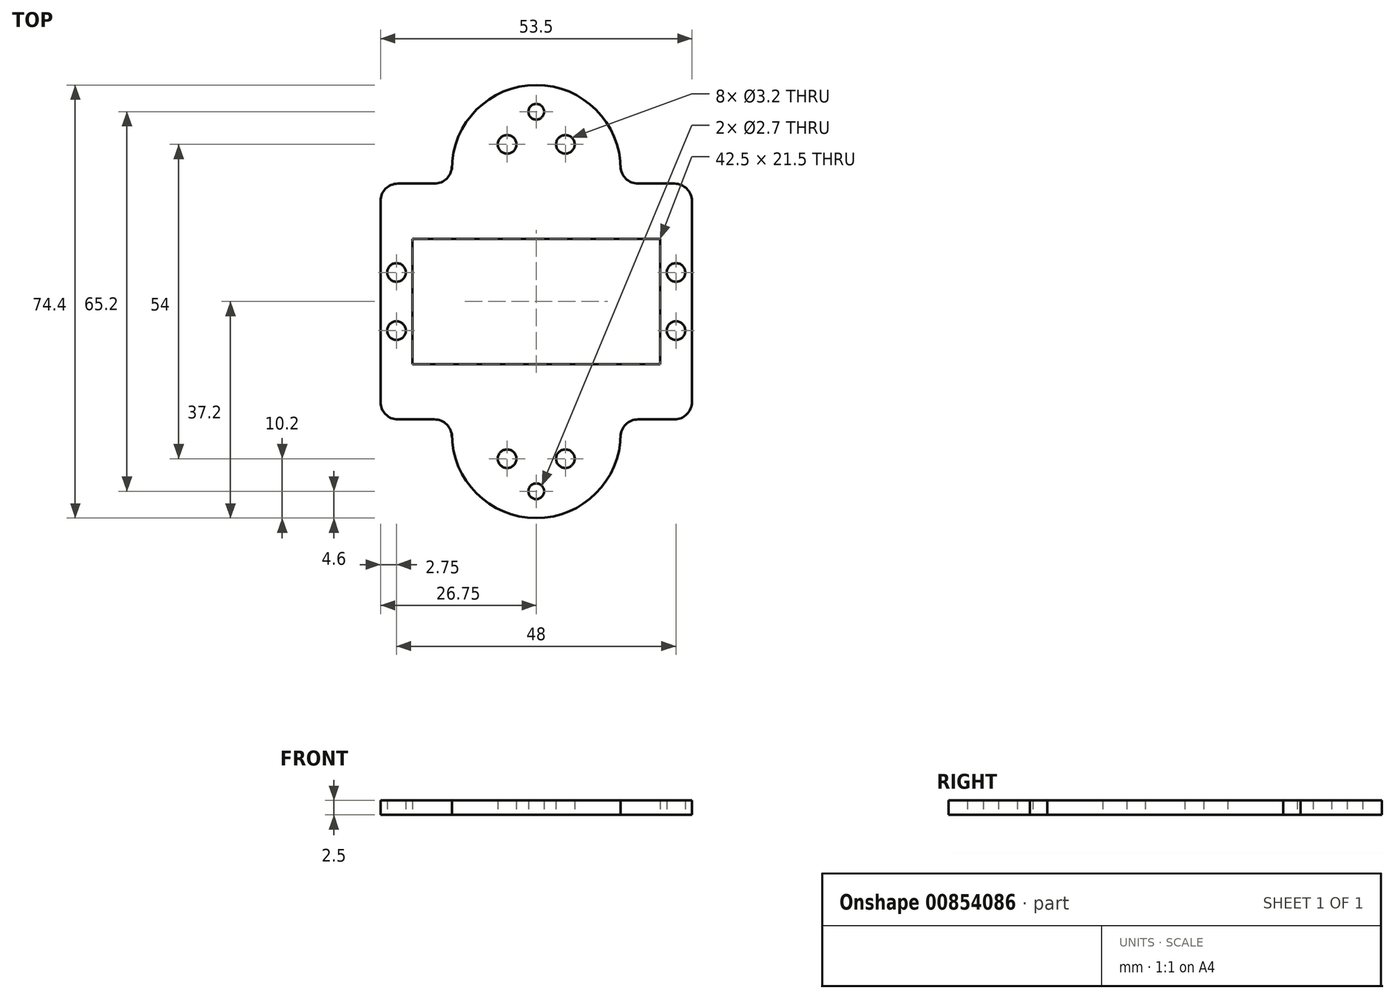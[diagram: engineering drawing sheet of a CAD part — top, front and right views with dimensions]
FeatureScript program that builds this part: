
annotation { "Feature Type Name" : "Feature", "Feature Type Description" : "" }
export const myFeature = defineFeature(function(context is Context, id is Id, definition is map)
    precondition{}
    {
        {
            var Q0;
            Q0=qCreatedBy(makeId("Top.planeOp"),FACE);
            var sketch = newSketch(context, id + "F0", { "sketchPlane" : qUnion([Q0])});
            skLineSegment(sketch, "E0", {"start": v(0, 0) * mm, "end": v(53.5, 0) * mm});
            skLineSegment(sketch, "E1", {"start": v(0, 0) * mm, "end": v(0, 17.25) * mm});
            skLineSegment(sketch, "E2", {"start": v(3, 20.25) * mm, "end": v(9.25, 20.25) * mm});
            skLineSegment(sketch, "E3", {"start": v(12.25, 22.7) * mm, "end": v(12.25, 23.25) * mm});
            skLineSegment(sketch, "E4", {"start": v(26.75, -69.73) * mm, "end": v(26.75, 52.22) * mm});
            skLineSegment(sketch, "E5", {"start": v(12.25, 22.7) * mm, "end": v(26.75, 22.7) * mm});
            skLineSegment(sketch, "E6.MirrorCS", {"start": v(53.5, 0) * mm, "end": v(53.5, 17.25) * mm});
            skLineSegment(sketch, "E7.MirrorCS", {"start": v(50.5, 20.25) * mm, "end": v(44.25, 20.25) * mm});
            skLineSegment(sketch, "E8.MirrorCS", {"start": v(41.25, 22.7) * mm, "end": v(41.25, 23.25) * mm});
            skLineSegment(sketch, "E9.MirrorCS", {"start": v(41.25, 22.7) * mm, "end": v(26.75, 22.7) * mm});
            skLineSegment(sketch, "E10.MirrorCS", {"start": v(0, 0) * mm, "end": v(0, -17.25) * mm});
            skLineSegment(sketch, "E11.MirrorCS", {"start": v(3, -20.25) * mm, "end": v(9.25, -20.25) * mm});
            skLineSegment(sketch, "E12.MirrorCS", {"start": v(12.25, -22.7) * mm, "end": v(12.25, -23.25) * mm});
            skLineSegment(sketch, "E13.MirrorCS", {"start": v(12.25, -22.7) * mm, "end": v(26.75, -22.7) * mm});
            skLineSegment(sketch, "E14.MirrorCS", {"start": v(41.25, -22.7) * mm, "end": v(26.75, -22.7) * mm});
            skLineSegment(sketch, "E15.MirrorCS", {"start": v(50.5, -20.25) * mm, "end": v(44.25, -20.25) * mm});
            skLineSegment(sketch, "E16.MirrorCS", {"start": v(53.5, 0) * mm, "end": v(53.5, -17.25) * mm});
            skLineSegment(sketch, "E17.MirrorCS", {"start": v(41.25, -22.7) * mm, "end": v(41.25, -23.25) * mm});
            skLineSegment(sketch, "E18", {"start": v(5.5, 0) * mm, "end": v(5.5, 10.75) * mm});
            skLineSegment(sketch, "E19", {"start": v(5.5, 10.75) * mm, "end": v(26.75, 10.75) * mm});
            skLineSegment(sketch, "E20.MirrorCS", {"start": v(48, 10.75) * mm, "end": v(26.75, 10.75) * mm});
            skLineSegment(sketch, "E21.MirrorCS", {"start": v(48, 0) * mm, "end": v(48, 10.75) * mm});
            skLineSegment(sketch, "E22.MirrorCS", {"start": v(5.5, 0) * mm, "end": v(5.5, -10.75) * mm});
            skLineSegment(sketch, "E23.MirrorCS", {"start": v(5.5, -10.75) * mm, "end": v(26.75, -10.75) * mm});
            skLineSegment(sketch, "E24.MirrorCS", {"start": v(48, -10.75) * mm, "end": v(26.75, -10.75) * mm});
            skLineSegment(sketch, "E25.MirrorCS", {"start": v(48, 0) * mm, "end": v(48, -10.75) * mm});
            skArc(sketch, "E26", {"start": v(41.25, 22.7) * mm, "mid": v(26.75, 37.2) * mm, "end": v(12.25, 22.7) * mm});
            skArc(sketch, "E27.MirrorCS", {"start": v(41.25, -22.7) * mm, "mid": v(26.75, -37.2) * mm, "end": v(12.25, -22.7) * mm});
            skCircle(sketch, "E28", {"center": v(2.75, 5) * mm, "radius": 1.6 * mm});
            skCircle(sketch, "E29.MirrorC", {"center": v(50.75, 5) * mm, "radius": 1.6 * mm});
            skCircle(sketch, "E30.MirrorC", {"center": v(2.75, -5) * mm, "radius": 1.6 * mm});
            skCircle(sketch, "E31.MirrorC", {"center": v(50.75, -5) * mm, "radius": 1.6 * mm});
            skCircle(sketch, "E32", {"center": v(21.75, 27) * mm, "radius": 1.6 * mm});
            skCircle(sketch, "E33.MirrorC", {"center": v(21.75, -27) * mm, "radius": 1.6 * mm});
            skCircle(sketch, "E34.MirrorC", {"center": v(31.75, 27) * mm, "radius": 1.6 * mm});
            skCircle(sketch, "E35.MirrorC", {"center": v(31.75, -27) * mm, "radius": 1.6 * mm});
            skCircle(sketch, "E36", {"center": v(26.75, 32.6) * mm, "radius": 1.35 * mm});
            skCircle(sketch, "E37.MirrorC", {"center": v(26.75, -32.6) * mm, "radius": 1.35 * mm});
            skPoint(sketch, "E38.visualSharp", {"position": v(0, -20.25) * mm});
            skArc(sketch, "E38.filletArc", {"start": v(0, -17.25) * mm, "mid": v(0.88, -19.37) * mm, "end": v(3, -20.25) * mm});
            skPoint(sketch, "E39.visualSharp", {"position": v(0, 20.25) * mm});
            skArc(sketch, "E39.filletArc", {"start": v(3, 20.25) * mm, "mid": v(0.88, 19.37) * mm, "end": v(0, 17.25) * mm});
            skPoint(sketch, "E40.visualSharp", {"position": v(12.25, 20.25) * mm});
            skArc(sketch, "E40.filletArc", {"start": v(9.25, 20.25) * mm, "mid": v(11.37, 21.13) * mm, "end": v(12.25, 23.25) * mm});
            skPoint(sketch, "E41.visualSharp", {"position": v(41.25, 20.25) * mm});
            skArc(sketch, "E41.filletArc", {"start": v(41.25, 23.25) * mm, "mid": v(42.13, 21.13) * mm, "end": v(44.25, 20.25) * mm});
            skPoint(sketch, "E42.visualSharp", {"position": v(53.5, 20.25) * mm});
            skArc(sketch, "E42.filletArc", {"start": v(53.5, 17.25) * mm, "mid": v(52.62, 19.37) * mm, "end": v(50.5, 20.25) * mm});
            skPoint(sketch, "E43.visualSharp", {"position": v(53.5, -20.25) * mm});
            skArc(sketch, "E43.filletArc", {"start": v(50.5, -20.25) * mm, "mid": v(52.62, -19.37) * mm, "end": v(53.5, -17.25) * mm});
            skPoint(sketch, "E44.visualSharp", {"position": v(41.25, -20.25) * mm});
            skArc(sketch, "E44.filletArc", {"start": v(44.25, -20.25) * mm, "mid": v(42.13, -21.13) * mm, "end": v(41.25, -23.25) * mm});
            skPoint(sketch, "E45.visualSharp", {"position": v(12.25, -20.25) * mm});
            skArc(sketch, "E45.filletArc", {"start": v(12.25, -23.25) * mm, "mid": v(11.37, -21.13) * mm, "end": v(9.25, -20.25) * mm});
            skSolve(sketch);
        }
        {
            var Q0;
            Q0=qSketchRegion(id+"F0",true);
            extrude(context, id + "F1", {"entities" : qUnion([Q0]), "depth" : 2.5 * mm, "offsetDistance" : 25 * mm});
        }
    });
